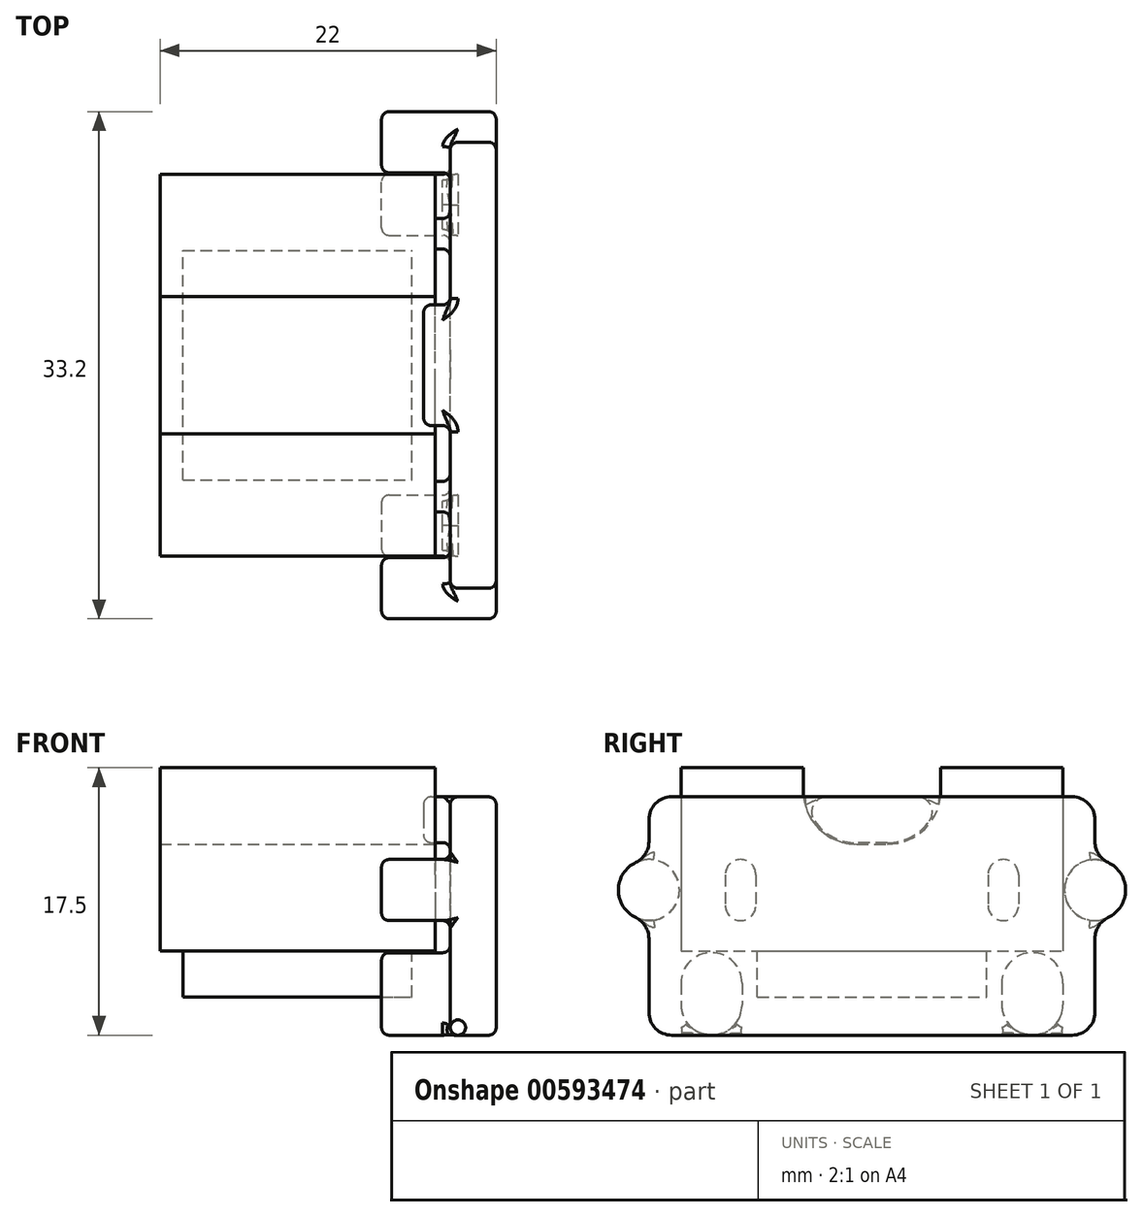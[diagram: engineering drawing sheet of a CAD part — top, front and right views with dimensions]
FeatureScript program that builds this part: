
annotation { "Feature Type Name" : "Feature", "Feature Type Description" : "" }
export const myFeature = defineFeature(function(context is Context, id is Id, definition is map)
    precondition{}
    {
        {
            var Q0;
            Q0=qCreatedBy(makeId("Top.planeOp"),FACE);
            var sketch = newSketch(context, id + "F0", { "sketchPlane" : qUnion([Q0])});
            skLineSegment(sketch, "E0.bottom", {"start": v(9, -12.5) * mm, "end": v(-9, -12.5) * mm});
            skLineSegment(sketch, "E0.top", {"start": v(9, 12.5) * mm, "end": v(-9, 12.5) * mm});
            skLineSegment(sketch, "E0.left", {"start": v(9, -12.5) * mm, "end": v(9, 12.5) * mm});
            skLineSegment(sketch, "E0.right", {"start": v(-9, -12.5) * mm, "end": v(-9, 12.5) * mm});
            skPoint(sketch, "E0.middle", {"position": v(0, 0) * mm});
            skSolve(sketch);
        }
        {
            var Q0;
            Q0=qSketchRegion(id+"F0",true);
            extrude(context, id + "F1", {"entities" : qUnion([Q0]), "depth" : 4.5 * mm, "offsetDistance" : 25 * mm});
        }
        {
            var Q0;
            Q0=makeQuery(id+"F1.opExtrude","CAP_FACE",FACE,{"disambiguationData":[OSD([sQuery(id+"F0.wireOp",EDGE,"E0.bottom"),sQuery(id+"F0.wireOp",EDGE,"E0.top"),sQuery(id+"F0.wireOp",EDGE,"E0.left"),sQuery(id+"F0.wireOp",EDGE,"E0.right")])],"isStart":true});
            var sketch = newSketch(context, id + "F2", { "sketchPlane" : qUnion([Q0])});
            skLineSegment(sketch, "E1.bottom", {"start": v(-7.5, 7.5) * mm, "end": v(7.5, 7.5) * mm});
            skLineSegment(sketch, "E1.top", {"start": v(-7.5, -7.5) * mm, "end": v(7.5, -7.5) * mm});
            skLineSegment(sketch, "E1.left", {"start": v(-7.5, 7.5) * mm, "end": v(-7.5, -7.5) * mm});
            skLineSegment(sketch, "E1.right", {"start": v(7.5, 7.5) * mm, "end": v(7.5, -7.5) * mm});
            skPoint(sketch, "E1.middle", {"position": v(0, 0) * mm});
            skSolve(sketch);
        }
        {
            var Q0;
            Q0=qSketchRegion(id+"F2",true);
            extrude(context, id + "F3", {"entities" : qUnion([Q0]), "operationType" : NewBodyOperationType.ADD, "depth" : 3 * mm, "offsetDistance" : 25 * mm});
        }
        {
            var Q0;
            Q0=makeQuery(id+"F1.opExtrude","SWEPT_FACE",FACE,{"disambiguationData":[OSD([sQuery(id+"F0.wireOp",EDGE,"E0.left")])]});
            var sketch = newSketch(context, id + "F4", { "sketchPlane" : qUnion([Q0])});
            skLineSegment(sketch, "E2", {"start": v(-12.5, 4.5) * mm, "end": v(-12.5, 12) * mm});
            skLineSegment(sketch, "E3", {"start": v(-12.5, 12) * mm, "end": v(-4.5, 12) * mm});
            skArc(sketch, "E4", {"start": v(-4.5, 10.5) * mm, "mid": v(-3.47, 8.03) * mm, "end": v(-1, 7) * mm});
            skLineSegment(sketch, "E5", {"start": v(-12.5, 4.5) * mm, "end": v(0, 4.5) * mm});
            skLineSegment(sketch, "E6", {"start": v(0, 7) * mm, "end": v(-1, 7) * mm});
            skLineSegment(sketch, "E7", {"start": v(-4.5, 12) * mm, "end": v(-4.5, 10.5) * mm});
            skLineSegment(sketch, "E8.MirrorCS", {"start": v(0, 7) * mm, "end": v(1, 7) * mm});
            skArc(sketch, "E9.MirrorCS", {"start": v(4.5, 10.5) * mm, "mid": v(3.47, 8.03) * mm, "end": v(1, 7) * mm});
            skLineSegment(sketch, "E10.MirrorCS", {"start": v(4.5, 12) * mm, "end": v(4.5, 10.5) * mm});
            skLineSegment(sketch, "E11.MirrorCS", {"start": v(12.5, 12) * mm, "end": v(4.5, 12) * mm});
            skLineSegment(sketch, "E12.MirrorCS", {"start": v(12.5, 4.5) * mm, "end": v(12.5, 12) * mm});
            skLineSegment(sketch, "E13.MirrorCS", {"start": v(12.5, 4.5) * mm, "end": v(0, 4.5) * mm});
            skSolve(sketch);
        }
        {
            var Q0;
            Q0 = qSketchRegion(id + "F4", true);
            var Q1;
            Q1=makeQuery(id+"F1.opExtrude","SWEPT_FACE",FACE,{"disambiguationData":[OSD([sQuery(id+"F0.wireOp",EDGE,"E0.right")])]});
            extrude(context, id + "F5", {"entities" : qUnion([Q0]), "operationType" : NewBodyOperationType.ADD, "endBound" : BoundingType.UP_TO_SURFACE, "oppositeDirection" : true, "depth" : 25 * mm, "endBoundEntityFace" : qUnion([Q1]), "offsetDistance" : 25 * mm});
        }
        {
            var Q0;
            Q0=makeQuery(id+"F5.boolean.opBoolean","MERGE",FACE,{"derivedFrom":[makeQuery(id+"F1.opExtrude","SWEPT_FACE",FACE,{"disambiguationData":[OSD([sQuery(id+"F0.wireOp",EDGE,"E0.left")])]}),makeQuery(id+"F5.opExtrude","CAP_FACE",FACE,{"disambiguationData":[OSD([sQuery(id+"F4.wireOp",EDGE,"E2"),sQuery(id+"F4.wireOp",EDGE,"E3"),sQuery(id+"F4.wireOp",EDGE,"E4"),sQuery(id+"F4.wireOp",EDGE,"E5"),sQuery(id+"F4.wireOp",EDGE,"E6"),sQuery(id+"F4.wireOp",EDGE,"E7"),sQuery(id+"F4.wireOp",EDGE,"E8.MirrorCS"),sQuery(id+"F4.wireOp",EDGE,"E9.MirrorCS"),sQuery(id+"F4.wireOp",EDGE,"E10.MirrorCS"),sQuery(id+"F4.wireOp",EDGE,"E11.MirrorCS"),sQuery(id+"F4.wireOp",EDGE,"E12.MirrorCS"),sQuery(id+"F4.wireOp",EDGE,"E13.MirrorCS")])],"isStart":true})]});
            var sketch = newSketch(context, id + "F6", { "sketchPlane" : qUnion([Q0])});
            skArc(sketch, "E14", {"start": v(-3.76, 8.52) * mm, "mid": v(-2.55, 7.47) * mm, "end": v(-1, 7.1) * mm});
            skLineSegment(sketch, "E15", {"start": v(0, 7.1) * mm, "end": v(-1, 7.1) * mm});
            skPoint(sketch, "E15.startSnap0", {"position": v(0, 7) * mm});
            skArc(sketch, "E16", {"start": v(-2.95, 10.1) * mm, "mid": v(-3.84, 9.56) * mm, "end": v(-3.76, 8.52) * mm});
            skLineSegment(sketch, "E17", {"start": v(0, 10.1) * mm, "end": v(-2.95, 10.1) * mm});
            skLineSegment(sketch, "E18.MirrorCS", {"start": v(0, 10.1) * mm, "end": v(2.95, 10.1) * mm});
            skArc(sketch, "E19.MirrorCS", {"start": v(2.95, 10.1) * mm, "mid": v(3.84, 9.56) * mm, "end": v(3.76, 8.52) * mm});
            skArc(sketch, "E20.MirrorCS", {"start": v(3.76, 8.52) * mm, "mid": v(2.55, 7.47) * mm, "end": v(1, 7.1) * mm});
            skLineSegment(sketch, "E21.MirrorCS", {"start": v(0, 7.1) * mm, "end": v(1, 7.1) * mm});
            skSolve(sketch);
        }
        {
            var Q0;
            Q0=makeQuery(id+"F6.imprint","IMPRINT",FACE,{"disambiguationData":[TD([[makeQuery(id+"F6.imprint","IMPRINT",EDGE,{"derivedFrom":sQuery(id+"F6.wireOp",EDGE,"E14")}),1.0]])]});
            extrude(context, id + "F7", {"entities" : qUnion([Q0]), "oppositeDirection" : true, "depth" : 0.75 * mm, "offsetDistance" : 25 * mm, "hasSecondDirection" : true, "secondDirectionOppositeDirection" : false, "secondDirectionDepth" : 1 * mm});
        }
        {
            var Q0;
            Q0=makeQuery(id+"F7.opExtrude","CAP_FACE",FACE,{"disambiguationData":[OSD([sQuery(id+"F6.wireOp",EDGE,"E14"),sQuery(id+"F6.wireOp",EDGE,"E15"),sQuery(id+"F6.wireOp",EDGE,"E16"),sQuery(id+"F6.wireOp",EDGE,"E17"),sQuery(id+"F6.wireOp",EDGE,"E18.MirrorCS"),sQuery(id+"F6.wireOp",EDGE,"E19.MirrorCS"),sQuery(id+"F6.wireOp",EDGE,"E20.MirrorCS"),sQuery(id+"F6.wireOp",EDGE,"E21.MirrorCS")])],"isStart":true});
            var sketch = newSketch(context, id + "F8", { "sketchPlane" : qUnion([Q0])});
            skLineSegment(sketch, "E22.bottom", {"start": v(-14.6, 10.1) * mm, "end": v(14.6, 10.1) * mm});
            skLineSegment(sketch, "E22.top", {"start": v(-14.6, -5.5) * mm, "end": v(14.6, -5.5) * mm});
            skLineSegment(sketch, "E22.right", {"start": v(14.6, 10.1) * mm, "end": v(14.6, -5.5) * mm});
            skLineSegment(sketch, "E23.MirrorCS", {"start": v(-14.6, 10.1) * mm, "end": v(-14.6, -5.5) * mm});
            skSolve(sketch);
        }
        {
            var Q0;
            Q0 = qSketchRegion(id + "F8", true);
            extrude(context, id + "F9", {"entities" : qUnion([Q0]), "operationType" : NewBodyOperationType.ADD, "depth" : 3 * mm, "offsetDistance" : 25 * mm});
        }
        {
            var Q0;
            Q0=makeQuery(id+"F9.opExtrude","CAP_FACE",FACE,{"disambiguationData":[OSD([sQuery(id+"F8.wireOp",EDGE,"E22.bottom"),sQuery(id+"F8.wireOp",EDGE,"E22.top"),sQuery(id+"F8.wireOp",EDGE,"E22.left"),sQuery(id+"F8.wireOp",EDGE,"E22.right")])],"isStart":true});
            var sketch = newSketch(context, id + "F10", { "sketchPlane" : qUnion([Q0])});
            skLineSegment(sketch, "E24.left", {"start": v(-12.5, -2.1) * mm, "end": v(-12.5, -3.5) * mm});
            skLineSegment(sketch, "E24.right", {"start": v(-8.5, -2.1) * mm, "end": v(-8.5, -3.5) * mm});
            skArc(sketch, "E25", {"start": v(-12.5, -3.5) * mm, "mid": v(-10.5, -5.5) * mm, "end": v(-8.5, -3.5) * mm});
            skArc(sketch, "E26", {"start": v(-8.5, -2.1) * mm, "mid": v(-10.5, -0.1) * mm, "end": v(-12.5, -2.1) * mm});
            skArc(sketch, "E27.MirrorCS", {"start": v(8.5, -2.1) * mm, "mid": v(10.5, -0.1) * mm, "end": v(12.5, -2.1) * mm});
            skLineSegment(sketch, "E28.MirrorCS", {"start": v(12.5, -2.1) * mm, "end": v(12.5, -3.5) * mm});
            skArc(sketch, "E29.MirrorCS", {"start": v(12.5, -3.5) * mm, "mid": v(10.5, -5.5) * mm, "end": v(8.5, -3.5) * mm});
            skLineSegment(sketch, "E30.MirrorCS", {"start": v(8.5, -2.1) * mm, "end": v(8.5, -3.5) * mm});
            skSolve(sketch);
        }
        {
            var Q0;
            Q0 = qSketchRegion(id + "F10", true);
            extrude(context, id + "F11", {"entities" : qUnion([Q0]), "operationType" : NewBodyOperationType.ADD, "depth" : 4.5 * mm, "offsetDistance" : 25 * mm});
        }
        {
            var Q0;
            Q0=makeQuery(id+"F9.opExtrude","CAP_FACE",FACE,{"disambiguationData":[OSD([sQuery(id+"F8.wireOp",EDGE,"E22.bottom"),sQuery(id+"F8.wireOp",EDGE,"E22.top"),sQuery(id+"F8.wireOp",EDGE,"E22.right"),sQuery(id+"F8.wireOp",EDGE,"E23.MirrorCS")])],"isStart":false});
            var sketch = newSketch(context, id + "F12", { "sketchPlane" : qUnion([Q0])});
            skCircle(sketch, "E31", {"center": v(14.6, 4) * mm, "radius": 2 * mm});
            skCircle(sketch, "E32.MirrorC", {"center": v(-14.6, 4) * mm, "radius": 2 * mm});
            skSolve(sketch);
        }
        {
            var Q0;
            Q0 = qSketchRegion(id + "F12", true);
            var Q1;
            Q1=makeQuery(id+"F11.opExtrude","CAP_FACE",FACE,{"disambiguationData":[OSD([sQuery(id+"F10.wireOp",EDGE,"E24.bottom"),sQuery(id+"F10.wireOp",EDGE,"E24.top"),sQuery(id+"F10.wireOp",EDGE,"E24.left"),sQuery(id+"F10.wireOp",EDGE,"E24.right")])],"isStart":false});
            extrude(context, id + "F13", {"entities" : qUnion([Q0]), "operationType" : NewBodyOperationType.ADD, "endBound" : BoundingType.UP_TO_SURFACE, "oppositeDirection" : true, "depth" : 25 * mm, "endBoundEntityFace" : qUnion([Q1]), "offsetDistance" : 25 * mm});
        }
        {
            var Q0;
            Q0=makeQuery(id+"F9.opExtrude","CAP_FACE",FACE,{"disambiguationData":[OSD([sQuery(id+"F8.wireOp",EDGE,"E22.bottom"),sQuery(id+"F8.wireOp",EDGE,"E22.top"),sQuery(id+"F8.wireOp",EDGE,"E22.right"),sQuery(id+"F8.wireOp",EDGE,"E23.MirrorCS")])],"isStart":true});
            var sketch = newSketch(context, id + "F14", { "sketchPlane" : qUnion([Q0])});
            skArc(sketch, "E33", {"start": v(-9.6, 3) * mm, "mid": v(-8.6, 2) * mm, "end": v(-7.6, 3) * mm});
            skLineSegment(sketch, "E34", {"start": v(-14.6, 2) * mm, "end": v(-8.6, 2) * mm, "construction": true});
            skLineSegment(sketch, "E35", {"start": v(-14.6, 6) * mm, "end": v(-8.6, 6) * mm, "construction": true});
            skArc(sketch, "E36", {"start": v(-7.6, 5) * mm, "mid": v(-8.6, 6) * mm, "end": v(-9.6, 5) * mm});
            skLineSegment(sketch, "E37", {"start": v(-9.6, 5) * mm, "end": v(-9.6, 3) * mm});
            skLineSegment(sketch, "E38", {"start": v(-7.6, 5) * mm, "end": v(-7.6, 3) * mm});
            skArc(sketch, "E39.MirrorCS", {"start": v(7.6, 5) * mm, "mid": v(8.6, 6) * mm, "end": v(9.6, 5) * mm});
            skLineSegment(sketch, "E40.MirrorCS", {"start": v(7.6, 5) * mm, "end": v(7.6, 3) * mm});
            skArc(sketch, "E41.MirrorCS", {"start": v(9.6, 3) * mm, "mid": v(8.6, 2) * mm, "end": v(7.6, 3) * mm});
            skLineSegment(sketch, "E42.MirrorCS", {"start": v(9.6, 5) * mm, "end": v(9.6, 3) * mm});
            skSolve(sketch);
        }
        {
            var Q0;
            Q0 = qSketchRegion(id + "F14", true);
            var Q1;
            Q1=makeQuery(id+"F5.boolean.opBoolean","MERGE",FACE,{"derivedFrom":[makeQuery(id+"F1.opExtrude","SWEPT_FACE",FACE,{"disambiguationData":[OSD([sQuery(id+"F0.wireOp",EDGE,"E0.left")])]}),makeQuery(id+"F5.opExtrude","CAP_FACE",FACE,{"disambiguationData":[OSD([sQuery(id+"F4.wireOp",EDGE,"E2"),sQuery(id+"F4.wireOp",EDGE,"E3"),sQuery(id+"F4.wireOp",EDGE,"E4"),sQuery(id+"F4.wireOp",EDGE,"E5"),sQuery(id+"F4.wireOp",EDGE,"E6"),sQuery(id+"F4.wireOp",EDGE,"E7"),sQuery(id+"F4.wireOp",EDGE,"E8.MirrorCS"),sQuery(id+"F4.wireOp",EDGE,"E9.MirrorCS"),sQuery(id+"F4.wireOp",EDGE,"E10.MirrorCS"),sQuery(id+"F4.wireOp",EDGE,"E11.MirrorCS"),sQuery(id+"F4.wireOp",EDGE,"E12.MirrorCS"),sQuery(id+"F4.wireOp",EDGE,"E13.MirrorCS")])],"isStart":true})]});
            extrude(context, id + "F15", {"entities" : qUnion([Q0]), "operationType" : NewBodyOperationType.ADD, "endBound" : BoundingType.UP_TO_SURFACE, "depth" : 0.8 * mm, "endBoundEntityFace" : qUnion([Q1]), "offsetDistance" : 25 * mm});
        }
        {
            var Q0;
            {var subQ0=sQuery(id+"F8.wireOp",EDGE,"E22.right");var subQ1=sQuery(id+"F12.wireOp",EDGE,"tLYUXB0z-z68I-CTtY-IskT-hRGRSvwDTnPy.bottom");Q0=makeQuery(id+"F13.boolean.opBoolean","SPLIT",EDGE,{"disambiguationData":[topologyDisambiguationEdgeConnected([makeQuery(id+"F9.opExtrude","SWEPT_FACE",FACE,{"disambiguationData":[OSD([subQ0])]})])],"derivedFrom":makeQuery(id+"F13.opExtrude","SWEPT_EDGE",EDGE,{"disambiguationData":[OSD([subQ0,subQ1,sQuery(id+"F12.wireOp",EDGE,"tLYUXB0z-z68I-CTtY-IskT-hRGRSvwDTnPy.left")])]})});}
            var Q1;
            {var subQ0=sQuery(id+"F8.wireOp",EDGE,"E22.right");var subQ1=sQuery(id+"F12.wireOp",EDGE,"tLYUXB0z-z68I-CTtY-IskT-hRGRSvwDTnPy.top");Q1=makeQuery(id+"F13.boolean.opBoolean","SPLIT",EDGE,{"disambiguationData":[topologyDisambiguationEdgeConnected([makeQuery(id+"F9.opExtrude","SWEPT_FACE",FACE,{"disambiguationData":[OSD([subQ0])]})])],"derivedFrom":makeQuery(id+"F13.opExtrude","SWEPT_EDGE",EDGE,{"disambiguationData":[OSD([subQ0,subQ1,sQuery(id+"F12.wireOp",EDGE,"tLYUXB0z-z68I-CTtY-IskT-hRGRSvwDTnPy.left")])]})});}
            var Q2;
            {var subQ0=sQuery(id+"F8.wireOp",EDGE,"E23.MirrorCS");var subQ1=sQuery(id+"F12.wireOp",EDGE,"42913ee7-faf4-44f0-98fc-0228379c075f0.MirrorCS");Q2=makeQuery(id+"F13.boolean.opBoolean","SPLIT",EDGE,{"disambiguationData":[topologyDisambiguationEdgeConnected([makeQuery(id+"F9.opExtrude","SWEPT_FACE",FACE,{"disambiguationData":[OSD([subQ0])]})])],"derivedFrom":makeQuery(id+"F13.opExtrude","SWEPT_EDGE",EDGE,{"disambiguationData":[OSD([subQ0,subQ1,sQuery(id+"F12.wireOp",EDGE,"95e365d9-dce3-4151-8750-6379b8add9b40.MirrorCS")])]})});}
            var Q3;
            {var subQ0=sQuery(id+"F8.wireOp",EDGE,"E23.MirrorCS");var subQ1=sQuery(id+"F12.wireOp",EDGE,"27367417-b79b-4e2b-9d2a-07c9ed3767140.MirrorCS");Q3=makeQuery(id+"F13.boolean.opBoolean","SPLIT",EDGE,{"disambiguationData":[topologyDisambiguationEdgeConnected([makeQuery(id+"F9.opExtrude","SWEPT_FACE",FACE,{"disambiguationData":[OSD([subQ0])]})])],"derivedFrom":makeQuery(id+"F13.opExtrude","SWEPT_EDGE",EDGE,{"disambiguationData":[OSD([subQ0,subQ1,sQuery(id+"F12.wireOp",EDGE,"95e365d9-dce3-4151-8750-6379b8add9b40.MirrorCS")])]})});}
            var Q4;
            Q4=makeQuery(id+"F9.opExtrude","SWEPT_EDGE",EDGE,{"disambiguationData":[OSD([sQuery(id+"F8.wireOp",EDGE,"E22.bottom"),sQuery(id+"F8.wireOp",EDGE,"E23.MirrorCS")])]});
            var Q5;
            Q5=makeQuery(id+"F9.opExtrude","SWEPT_EDGE",EDGE,{"disambiguationData":[OSD([sQuery(id+"F8.wireOp",EDGE,"E22.bottom"),sQuery(id+"F8.wireOp",EDGE,"E22.right")])]});
            var Q6;
            Q6=makeQuery(id+"F13.opExtrude","SWEPT_EDGE",EDGE,{"disambiguationData":[OSD([sQuery(id+"F12.wireOp",EDGE,"tLYUXB0z-z68I-CTtY-IskT-hRGRSvwDTnPy.bottom"),sQuery(id+"F12.wireOp",EDGE,"tLYUXB0z-z68I-CTtY-IskT-hRGRSvwDTnPy.right")])]});
            var Q7;
            Q7=makeQuery(id+"F13.opExtrude","SWEPT_EDGE",EDGE,{"disambiguationData":[OSD([sQuery(id+"F12.wireOp",EDGE,"tLYUXB0z-z68I-CTtY-IskT-hRGRSvwDTnPy.top"),sQuery(id+"F12.wireOp",EDGE,"tLYUXB0z-z68I-CTtY-IskT-hRGRSvwDTnPy.right")])]});
            var Q8;
            Q8=makeQuery(id+"F13.opExtrude","SWEPT_EDGE",EDGE,{"disambiguationData":[OSD([sQuery(id+"F12.wireOp",EDGE,"42913ee7-faf4-44f0-98fc-0228379c075f0.MirrorCS"),sQuery(id+"F12.wireOp",EDGE,"89a3b5b5-859e-4bdd-b88f-204a61816cf10.MirrorCS")])]});
            var Q9;
            Q9=makeQuery(id+"F13.opExtrude","SWEPT_EDGE",EDGE,{"disambiguationData":[OSD([sQuery(id+"F12.wireOp",EDGE,"89a3b5b5-859e-4bdd-b88f-204a61816cf10.MirrorCS"),sQuery(id+"F12.wireOp",EDGE,"27367417-b79b-4e2b-9d2a-07c9ed3767140.MirrorCS")])]});
            var Q10;
            Q10=makeQuery(id+"F13.opExtrude","TWEAK_EDGE",EDGE,{"derivedFrom":[makeQuery(id+"F11.opExtrude","CAP_FACE",FACE,{"disambiguationData":[OSD([sQuery(id+"F10.wireOp",EDGE,"E24.bottom"),sQuery(id+"F10.wireOp",EDGE,"E24.top"),sQuery(id+"F10.wireOp",EDGE,"E24.left"),sQuery(id+"F10.wireOp",EDGE,"E24.right")])],"isStart":false}),makeQuery(id+"F12.imprint","IMPRINT",EDGE,{"derivedFrom":sQuery(id+"F12.wireOp",EDGE,"tLYUXB0z-z68I-CTtY-IskT-hRGRSvwDTnPy.left")})]});
            var Q11;
            Q11=makeQuery(id+"F13.opExtrude","TWEAK_EDGE",EDGE,{"derivedFrom":[makeQuery(id+"F11.opExtrude","CAP_FACE",FACE,{"disambiguationData":[OSD([sQuery(id+"F10.wireOp",EDGE,"E24.bottom"),sQuery(id+"F10.wireOp",EDGE,"E24.top"),sQuery(id+"F10.wireOp",EDGE,"E24.left"),sQuery(id+"F10.wireOp",EDGE,"E24.right")])],"isStart":false}),makeQuery(id+"F12.imprint","IMPRINT",EDGE,{"derivedFrom":sQuery(id+"F12.wireOp",EDGE,"95e365d9-dce3-4151-8750-6379b8add9b40.MirrorCS")})]});
            var Q12;
            Q12=makeQuery(id+"F11.opExtrude","CAP_EDGE",EDGE,{"disambiguationData":[OSD([sQuery(id+"F10.wireOp",EDGE,"E24.bottom")])],"isStart":false});
            var Q13;
            Q13=makeQuery(id+"F11.opExtrude","CAP_EDGE",EDGE,{"disambiguationData":[OSD([sQuery(id+"F10.wireOp",EDGE,"a4e23ce9-4728-4595-89ca-8bbff5c4f8e50.MirrorCS")])],"isStart":false});
            var Q14;
            Q14=makeQuery(id+"F13.boolean.opBoolean","INTERSECT",EDGE,{"disambiguationData":[OD(0.0)],"derivedFrom":[makeQuery(id+"F9.opExtrude","SWEPT_FACE",FACE,{"disambiguationData":[OSD([sQuery(id+"F8.wireOp",EDGE,"E22.right")])]}),makeQuery(id+"F13.opExtrude","SWEPT_FACE",FACE,{"disambiguationData":[OSD([sQuery(id+"F12.wireOp",EDGE,"E31")])]})]});
            var Q15;
            Q15=makeQuery(id+"F13.boolean.opBoolean","INTERSECT",EDGE,{"disambiguationData":[OD(1.0)],"derivedFrom":[makeQuery(id+"F9.opExtrude","SWEPT_FACE",FACE,{"disambiguationData":[OSD([sQuery(id+"F8.wireOp",EDGE,"E22.right")])]}),makeQuery(id+"F13.opExtrude","SWEPT_FACE",FACE,{"disambiguationData":[OSD([sQuery(id+"F12.wireOp",EDGE,"E31")])]})]});
            var Q16;
            Q16=makeQuery(id+"F13.boolean.opBoolean","INTERSECT",EDGE,{"disambiguationData":[OD(0.0)],"derivedFrom":[makeQuery(id+"F9.opExtrude","SWEPT_FACE",FACE,{"disambiguationData":[OSD([sQuery(id+"F8.wireOp",EDGE,"E23.MirrorCS")])]}),makeQuery(id+"F13.opExtrude","SWEPT_FACE",FACE,{"disambiguationData":[OSD([sQuery(id+"F12.wireOp",EDGE,"E32.MirrorC")])]})]});
            var Q17;
            Q17=makeQuery(id+"F13.boolean.opBoolean","INTERSECT",EDGE,{"disambiguationData":[OD(1.0)],"derivedFrom":[makeQuery(id+"F9.opExtrude","SWEPT_FACE",FACE,{"disambiguationData":[OSD([sQuery(id+"F8.wireOp",EDGE,"E23.MirrorCS")])]}),makeQuery(id+"F13.opExtrude","SWEPT_FACE",FACE,{"disambiguationData":[OSD([sQuery(id+"F12.wireOp",EDGE,"E32.MirrorC")])]})]});
            var Q18;
            Q18=makeQuery(id+"F9.opExtrude","SWEPT_EDGE",EDGE,{"disambiguationData":[OSD([sQuery(id+"F8.wireOp",EDGE,"E22.top"),sQuery(id+"F8.wireOp",EDGE,"E22.right")])]});
            var Q19;
            Q19=makeQuery(id+"F9.opExtrude","SWEPT_EDGE",EDGE,{"disambiguationData":[OSD([sQuery(id+"F8.wireOp",EDGE,"E22.top"),sQuery(id+"F8.wireOp",EDGE,"E23.MirrorCS")])]});
            fillet(context, id + "F16", {"entities" : qUnion([Q0, Q1, Q2, Q3, Q4, Q5, Q6, Q7, Q8, Q9, Q10, Q11, Q12, Q13, Q14, Q15, Q16, Q17, Q18, Q19]), "radius" : 1.5 * mm, "tangentPropagation" : true, "allowEdgeOverflow" : false});
        }
        {
            var Q0;
            Q0=makeQuery(id+"F9.opExtrude","CAP_EDGE",EDGE,{"disambiguationData":[OSD([sQuery(id+"F8.wireOp",EDGE,"E22.top")])],"isStart":false});
            var Q1;
            Q1=makeQuery(id+"F9.opExtrude","CAP_FACE",FACE,{"disambiguationData":[OSD([sQuery(id+"F8.wireOp",EDGE,"E22.bottom"),sQuery(id+"F8.wireOp",EDGE,"E22.top"),sQuery(id+"F8.wireOp",EDGE,"E22.right"),sQuery(id+"F8.wireOp",EDGE,"E23.MirrorCS")])],"isStart":true});
            var Q2;
            Q2=makeQuery(id+"F13.opExtrude","CAP_FACE",FACE,{"disambiguationData":[OSD([sQuery(id+"F12.wireOp",EDGE,"E31")])],"isStart":false});
            var Q3;
            Q3=makeQuery(id+"F11.opExtrude","CAP_FACE",FACE,{"disambiguationData":[OSD([sQuery(id+"F10.wireOp",EDGE,"E24.left"),sQuery(id+"F10.wireOp",EDGE,"E24.right"),sQuery(id+"F10.wireOp",EDGE,"E25"),sQuery(id+"F10.wireOp",EDGE,"E26")])],"isStart":false});
            var Q4;
            Q4=makeQuery(id+"F11.opExtrude","CAP_FACE",FACE,{"disambiguationData":[OSD([sQuery(id+"F10.wireOp",EDGE,"E27.MirrorCS"),sQuery(id+"F10.wireOp",EDGE,"E28.MirrorCS"),sQuery(id+"F10.wireOp",EDGE,"E29.MirrorCS"),sQuery(id+"F10.wireOp",EDGE,"E30.MirrorCS")])],"isStart":false});
            var Q5;
            Q5=makeQuery(id+"F13.opExtrude","CAP_FACE",FACE,{"disambiguationData":[OSD([sQuery(id+"F12.wireOp",EDGE,"E32.MirrorC")])],"isStart":false});
            var Q6;
            Q6=makeQuery(id+"F7.opExtrude","CAP_FACE",FACE,{"disambiguationData":[OSD([sQuery(id+"F6.wireOp",EDGE,"E14"),sQuery(id+"F6.wireOp",EDGE,"E15"),sQuery(id+"F6.wireOp",EDGE,"E16"),sQuery(id+"F6.wireOp",EDGE,"E17"),sQuery(id+"F6.wireOp",EDGE,"E18.MirrorCS"),sQuery(id+"F6.wireOp",EDGE,"E19.MirrorCS"),sQuery(id+"F6.wireOp",EDGE,"E20.MirrorCS"),sQuery(id+"F6.wireOp",EDGE,"E21.MirrorCS")])],"isStart":false});
            var Q7;
            Q7=makeQuery(id+"F15.opExtrude","CAP_FACE",FACE,{"disambiguationData":[OSD([sQuery(id+"F14.wireOp",EDGE,"E33"),sQuery(id+"F14.wireOp",EDGE,"E36"),sQuery(id+"F14.wireOp",EDGE,"E37"),sQuery(id+"F14.wireOp",EDGE,"E38")])],"isStart":false});
            var Q8;
            Q8=makeQuery(id+"F15.opExtrude","CAP_FACE",FACE,{"disambiguationData":[OSD([sQuery(id+"F14.wireOp",EDGE,"E39.MirrorCS"),sQuery(id+"F14.wireOp",EDGE,"E40.MirrorCS"),sQuery(id+"F14.wireOp",EDGE,"E41.MirrorCS"),sQuery(id+"F14.wireOp",EDGE,"E42.MirrorCS")])],"isStart":false});
            fillet(context, id + "F17", {"entities" : qUnion([Q0, Q1, Q2, Q3, Q4, Q5, Q6, Q7, Q8]), "radius" : 0.5 * mm, "tangentPropagation" : true, "allowEdgeOverflow" : false});
        }
    });
